# Revit family: Midea_FCU_two pipe 2th Ceiling&Floor MKH3-250R3(R4)(DC50,60Hz)-Floor
name_source: partatom
category: Mechanical Equipment
revit_build: Autodesk Revit 2013 (Build: 20120221_2030(x64)
units: mm (PartAtom-declared; Revit-internal decimal feet)

## types (2) — shared parameters
Circuit breaker = 15 A
Condensation = water
Description = High efficiency water cooled
Drain pipe = 18.5 mm  [stored 0.0606955 ft]
Height = 200 mm  [stored 0.656168 ft]
Installation = Indoor installation
Liquid pipe = 19.05 mm  [stored 0.0625 ft]
Machine material = Galvanized Steel
Manufacturer = Midea
Panel color = -
Power Input(H/M/L) = 47/26/14 W
Power supply = 220-240V ~50Hz/60Hz
Rated current = 0 A
Series = FCU
clearance access behind = 50 mm  [stored 0.164042 ft]
clearance access down = 90 mm  [stored 0.295276 ft]
clearance access left = 150 mm
clearance access right = 150 mm
clearance access up = 1500 mm  [stored 4.92126 ft]

## per-type parameters (varying)
| type | Air Flow(H/M/L) | Cooling Capacity(H/M/L) | Depth | Heating Capacity(H/M/L) | Net Weight | Width |
| MKH3-250-R3 | 400/273/180 m3/h | 2.65/2.02/1.40 kW | 1020 mm  [stored 3.34646 ft] | 3.05/2.24/1.52 kW | 13.90 kg | 495 mm  [stored 1.62402 ft] |
| MKH3-250-R4 | 425/284/184 m3/h | 3.05/2.26/1.63 kW | 858 mm  [stored 2.81496 ft] | 3.15/2.09/1.38 kW | 14.80 kg | 455 mm  [stored 1.49278 ft] |

note: column(s) folded — value = type name in every type: Model

note: [stored X ft] marks values corroborated as IEEE doubles in the binary element streams (Revit-internal decimal feet)

## geometry (parser evidence)
native form markers: Blend x2, Sweep x3
no freeform markers — native parametric forms only
